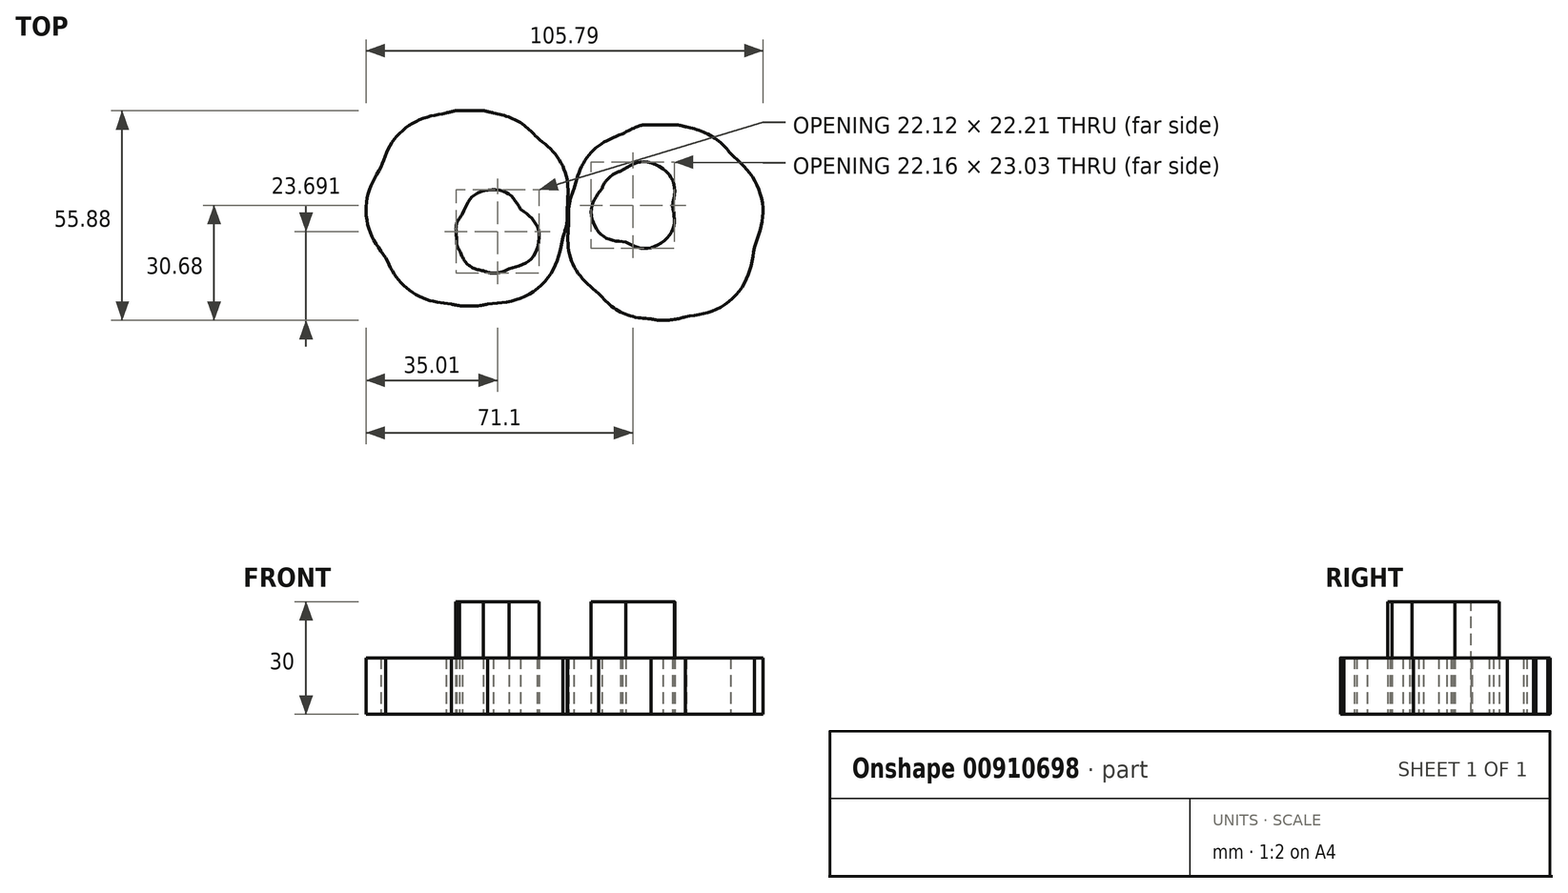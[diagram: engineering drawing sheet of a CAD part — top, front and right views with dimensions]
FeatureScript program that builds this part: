
annotation { "Feature Type Name" : "Feature", "Feature Type Description" : "" }
export const myFeature = defineFeature(function(context is Context, id is Id, definition is map)
    precondition{}
    {
        {
            var Q0;
            Q0=qCreatedBy(makeId("Top.planeOp"),FACE);
            var sketch = newSketch(context, id + "F0", { "sketchPlane" : qUnion([Q0])});
            skLineSegment(sketch, "E0", {"start": v(-95.48, 27.03) * mm, "end": v(-93.03, 29.79) * mm});
            skLineSegment(sketch, "E1", {"start": v(-93.03, 29.79) * mm, "end": v(-93.83, 30.39) * mm});
            skLineSegment(sketch, "E2", {"start": v(56.23, 54.56) * mm, "end": v(55.74, 53.41) * mm});
            skLineSegment(sketch, "E3", {"start": v(55.74, 53.41) * mm, "end": v(57.24, 52.44) * mm});
            skLineSegment(sketch, "E4", {"start": v(80.84, 41.38) * mm, "end": v(80.41, 40.74) * mm});
            skLineSegment(sketch, "E5", {"start": v(80.41, 40.74) * mm, "end": v(81.45, 40.47) * mm});
            skLineSegment(sketch, "E6", {"start": v(91.54, 26.28) * mm, "end": v(91, 26.08) * mm});
            skLineSegment(sketch, "E7", {"start": v(91, 26.08) * mm, "end": v(91.57, 24.93) * mm});
            skLineSegment(sketch, "E8", {"start": v(47.32, -84.2) * mm, "end": v(46.66, -83.57) * mm});
            skLineSegment(sketch, "E9", {"start": v(46.66, -83.57) * mm, "end": v(45.4, -85.45) * mm});
            skLineSegment(sketch, "E10", {"start": v(30.38, -92.46) * mm, "end": v(26.04, -92.61) * mm});
            skLineSegment(sketch, "E11", {"start": v(26.04, -92.61) * mm, "end": v(24.45, -94.1) * mm});
            skLineSegment(sketch, "E12", {"start": v(93.42, 9.92) * mm, "end": v(92.25, 12.13) * mm});
            skLineSegment(sketch, "E13", {"start": v(92.25, 12.13) * mm, "end": v(94.47, 11.99) * mm});
            skLineSegment(sketch, "E14", {"start": v(79.1, 38.53) * mm, "end": v(75.94, 39.15) * mm});
            skLineSegment(sketch, "E15", {"start": v(75.94, 39.15) * mm, "end": v(77.48, 40.95) * mm});
            skLineSegment(sketch, "E16", {"start": v(-43.97, 54.22) * mm, "end": v(-45.63, 56.72) * mm});
            skLineSegment(sketch, "E17", {"start": v(-45.63, 56.72) * mm, "end": v(-47.69, 56.87) * mm});
            skLineSegment(sketch, "E18", {"start": v(-94.6, 38.67) * mm, "end": v(-95.54, 38.86) * mm});
            skLineSegment(sketch, "E19", {"start": v(-95.54, 38.86) * mm, "end": v(-95.41, 37.43) * mm});
            skLineSegment(sketch, "E20", {"start": v(-81.53, -51.42) * mm, "end": v(-80.93, -50.2) * mm});
            skLineSegment(sketch, "E21", {"start": v(-80.93, -50.2) * mm, "end": v(-79.65, -54.72) * mm});
            skLineSegment(sketch, "E22", {"start": v(-52.24, -80.03) * mm, "end": v(-51.67, -79.57) * mm});
            skLineSegment(sketch, "E23", {"start": v(-51.67, -79.57) * mm, "end": v(-52.32, -78.88) * mm});
            skLineSegment(sketch, "E24", {"start": v(-83.46, 17.28) * mm, "end": v(-84.76, 19.09) * mm});
            skLineSegment(sketch, "E25", {"start": v(-84.76, 19.09) * mm, "end": v(-85.17, 18.4) * mm});
            skLineSegment(sketch, "E26", {"start": v(-83.81, 23.75) * mm, "end": v(-82.2, 23.79) * mm});
            skLineSegment(sketch, "E27", {"start": v(-82.2, 23.79) * mm, "end": v(-82.25, 21.9) * mm});
            skLineSegment(sketch, "E28", {"start": v(-34.26, 8.25) * mm, "end": v(-34.27, 7.59) * mm});
            skLineSegment(sketch, "E29", {"start": v(-34.27, 7.59) * mm, "end": v(-30.97, 7.59) * mm});
            skLineSegment(sketch, "E30", {"start": v(84.23, 4.65) * mm, "end": v(83.07, 5.79) * mm});
            skLineSegment(sketch, "E31", {"start": v(83.07, 5.79) * mm, "end": v(82.44, 4.95) * mm});
            skLineSegment(sketch, "E32", {"start": v(70.9, -1.37) * mm, "end": v(68.33, -1.9) * mm});
            skLineSegment(sketch, "E33", {"start": v(68.33, -1.9) * mm, "end": v(66.96, -4.53) * mm});
            skLineSegment(sketch, "E34", {"start": v(-1.99, -65.46) * mm, "end": v(-1.99, -65.46) * mm});
            skFitSpline(sketch, "E35", {"points": [v(6.05, -97.79) * mm, v(4.14, -97.5) * mm, v(2.63, -97.06) * mm, v(2.15, -96.63) * mm]});
            skFitSpline(sketch, "E36", {"points": [v(2.15, -96.63) * mm, v(1.78, -96.3) * mm, v(1.5, -96.31) * mm, v(-0.79, -96.78) * mm]});
            skFitSpline(sketch, "E37", {"points": [v(-0.79, -96.78) * mm, v(-5.54, -97.75) * mm, v(-11.38, -97.34) * mm, v(-19.87, -95.46) * mm]});
            skFitSpline(sketch, "E38", {"points": [v(-19.87, -95.46) * mm, v(-24.4, -94.46) * mm, v(-26.88, -93.53) * mm, v(-29.89, -91.7) * mm]});
            skFitSpline(sketch, "E39", {"points": [v(-29.89, -91.7) * mm, v(-31.74, -90.58) * mm, v(-32.75, -90.1) * mm, v(-33.02, -90.22) * mm]});
            skFitSpline(sketch, "E40", {"points": [v(-33.02, -90.22) * mm, v(-34.1, -90.66) * mm, v(-35.18, -90.77) * mm, v(-36.19, -90.53) * mm]});
            skFitSpline(sketch, "E41", {"points": [v(-36.19, -90.53) * mm, v(-38.87, -89.9) * mm, v(-43.88, -86.85) * mm, v(-47.32, -83.78) * mm]});
            skFitSpline(sketch, "E42", {"points": [v(-47.32, -83.78) * mm, v(-50.23, -81.18) * mm, v(-49.98, -81.3) * mm, v(-50.83, -82.01) * mm]});
            skFitSpline(sketch, "E43", {"points": [v(-50.83, -82.01) * mm, v(-51.67, -82.72) * mm, v(-53.21, -83.02) * mm, v(-54.97, -82.8) * mm]});
            skFitSpline(sketch, "E44", {"points": [v(-54.97, -82.8) * mm, v(-57.33, -82.53) * mm, v(-60.2, -80.23) * mm, v(-65.02, -74.79) * mm]});
            skFitSpline(sketch, "E45", {"points": [v(-65.02, -74.79) * mm, v(-66.5, -73.1) * mm, v(-67.85, -71.58) * mm, v(-68.02, -71.39) * mm]});
            skFitSpline(sketch, "E46", {"points": [v(-68.02, -71.39) * mm, v(-68.28, -71.1) * mm, v(-68.36, -71.14) * mm, v(-68.55, -71.63) * mm]});
            skFitSpline(sketch, "E47", {"points": [v(-68.55, -71.63) * mm, v(-69.1, -73.05) * mm, v(-70.94, -73.6) * mm, v(-72.26, -72.75) * mm]});
            skFitSpline(sketch, "E48", {"points": [v(-72.26, -72.75) * mm, v(-73.16, -72.16) * mm, v(-76.32, -68.49) * mm, v(-77.69, -66.44) * mm]});
            skFitSpline(sketch, "E49", {"points": [v(-77.69, -66.44) * mm, v(-78.97, -64.52) * mm, v(-79.65, -62.88) * mm, v(-81.02, -58.41) * mm]});
            skFitSpline(sketch, "E50", {"points": [v(-81.02, -58.41) * mm, v(-81.9, -55.54) * mm, v(-81.96, -55.4) * mm, v(-82.71, -55.16) * mm]});
            skFitSpline(sketch, "E51", {"points": [v(-82.71, -55.16) * mm, v(-83.82, -54.8) * mm, v(-84.43, -54.07) * mm, v(-86.12, -51.11) * mm]});
            skFitSpline(sketch, "E52", {"points": [v(-86.12, -51.11) * mm, v(-89.94, -44.44) * mm, v(-90.7, -41.83) * mm, v(-91.66, -32.31) * mm]});
            skFitSpline(sketch, "E53", {"points": [v(-91.66, -32.31) * mm, v(-91.82, -30.7) * mm, v(-92.03, -29.37) * mm, v(-92.12, -29.37) * mm]});
            skFitSpline(sketch, "E54", {"points": [v(-92.12, -29.37) * mm, v(-92.21, -29.37) * mm, v(-93.03, -29.8) * mm, v(-93.94, -30.32) * mm]});
            skFitSpline(sketch, "E55", {"points": [v(-93.94, -30.32) * mm, v(-95.84, -31.41) * mm, v(-99.04, -32.54) * mm, v(-100.23, -32.54) * mm]});
            skFitSpline(sketch, "E56", {"points": [v(-100.23, -32.54) * mm, v(-101.33, -32.54) * mm, v(-102.26, -31.8) * mm, v(-102.53, -30.72) * mm]});
            skFitSpline(sketch, "E57", {"points": [v(-102.53, -30.72) * mm, v(-102.74, -29.9) * mm, v(-102.63, -29.57) * mm, v(-101.04, -26.3) * mm]});
            skFitSpline(sketch, "E58", {"points": [v(-101.04, -26.3) * mm, v(-100.1, -24.36) * mm, v(-99.15, -22.23) * mm, v(-98.92, -21.57) * mm]});
            skFitSpline(sketch, "E59", {"points": [v(-98.92, -21.57) * mm, v(-98.32, -19.8) * mm, v(-98.43, -16.76) * mm, v(-99.29, -11.54) * mm]});
            skFitSpline(sketch, "E60", {"points": [v(-99.29, -11.54) * mm, v(-100.31, -5.31) * mm, v(-100.38, -4.25) * mm, v(-99.94, -1.18) * mm]});
            skFitSpline(sketch, "E61", {"points": [v(-99.94, -1.18) * mm, v(-99.74, 0.27) * mm, v(-99.6, 1.48) * mm, v(-99.65, 1.53) * mm]});
            skFitSpline(sketch, "E62", {"points": [v(-99.65, 1.53) * mm, v(-99.69, 1.57) * mm, v(-100.03, 1.48) * mm, v(-100.41, 1.34) * mm]});
            skFitSpline(sketch, "E63", {"points": [v(-100.41, 1.34) * mm, v(-101.82, 0.8) * mm, v(-103.37, 1.61) * mm, v(-103.71, 3.05) * mm]});
            skFitSpline(sketch, "E64", {"points": [v(-103.71, 3.05) * mm, v(-103.97, 4.14) * mm, v(-100.97, 17.98) * mm, v(-99.82, 21) * mm]});
            skFitSpline(sketch, "E65", {"points": [v(-99.82, 21) * mm, v(-99.22, 22.58) * mm, v(-98.33, 23.82) * mm, v(-95.48, 27.03) * mm]});
            skFitSpline(sketch, "E66", {"points": [v(-93.83, 30.39) * mm, v(-95.91, 31.94) * mm, v(-96.84, 33.33) * mm, v(-97.51, 35.92) * mm]});
            skFitSpline(sketch, "E67", {"points": [v(-97.51, 35.92) * mm, v(-98.3, 38.9) * mm, v(-97.56, 40.94) * mm, v(-95.7, 41) * mm]});
            skFitSpline(sketch, "E68", {"points": [v(-95.7, 41) * mm, v(-95.24, 41.03) * mm, v(-93.74, 40.9) * mm, v(-92.36, 40.72) * mm]});
            skFitSpline(sketch, "E69", {"points": [v(-92.36, 40.72) * mm, v(-87.83, 40.15) * mm, v(-83.3, 40.79) * mm, v(-79.67, 42.5) * mm]});
            skFitSpline(sketch, "E70", {"points": [v(-79.67, 42.5) * mm, v(-77.94, 43.33) * mm, v(-77.62, 43.83) * mm, v(-78.84, 43.83) * mm]});
            skFitSpline(sketch, "E71", {"points": [v(-78.84, 43.83) * mm, v(-79.85, 43.83) * mm, v(-81.26, 44.34) * mm, v(-81.8, 44.9) * mm]});
            skFitSpline(sketch, "E72", {"points": [v(-81.8, 44.9) * mm, v(-83.07, 46.27) * mm, v(-82.51, 48.3) * mm, v(-80.42, 49.94) * mm]});
            skFitSpline(sketch, "E73", {"points": [v(-80.42, 49.94) * mm, v(-76.42, 53.08) * mm, v(-71.34, 55.19) * mm, v(-66.49, 55.72) * mm]});
            skFitSpline(sketch, "E74", {"points": [v(-66.49, 55.72) * mm, v(-64.9, 55.9) * mm, v(-64.88, 55.92) * mm, v(-65.21, 57.34) * mm]});
            skFitSpline(sketch, "E75", {"points": [v(-65.21, 57.34) * mm, v(-65.65, 59.22) * mm, v(-63.92, 62.87) * mm, v(-62.2, 63.69) * mm]});
            skFitSpline(sketch, "E76", {"points": [v(-62.2, 63.69) * mm, v(-61.14, 64.2) * mm, v(-59.85, 63.92) * mm, v(-59.2, 63.04) * mm]});
            skFitSpline(sketch, "E77", {"points": [v(-59.2, 63.04) * mm, v(-58.54, 62.14) * mm, v(-55.62, 60.81) * mm, v(-52.6, 60.02) * mm]});
            skFitSpline(sketch, "E78", {"points": [v(-52.6, 60.02) * mm, v(-49.95, 59.34) * mm, v(-46.75, 58.98) * mm, v(-46.75, 59.36) * mm]});
            skFitSpline(sketch, "E79", {"points": [v(-46.75, 59.36) * mm, v(-46.75, 59.5) * mm, v(-46.92, 60.08) * mm, v(-47.12, 60.66) * mm]});
            skFitSpline(sketch, "E80", {"points": [v(-47.12, 60.66) * mm, v(-48.58, 64.8) * mm, v(-49, 71.08) * mm, v(-48.1, 75.27) * mm]});
            skFitSpline(sketch, "E81", {"points": [v(-48.1, 75.27) * mm, v(-47.2, 79.44) * mm, v(-45.9, 82.5) * mm, v(-43.58, 85.88) * mm]});
            skFitSpline(sketch, "E82", {"points": [v(-43.58, 85.88) * mm, v(-39.81, 91.4) * mm, v(-34.08, 95.4) * mm, v(-27.41, 97.16) * mm]});
            skFitSpline(sketch, "E83", {"points": [v(-27.41, 97.16) * mm, v(-24.72, 97.87) * mm, v(-24.3, 97.92) * mm, v(-20.35, 97.92) * mm]});
            skFitSpline(sketch, "E84", {"points": [v(-20.35, 97.92) * mm, v(-16.41, 97.92) * mm, v(-15.97, 97.87) * mm, v(-13.34, 97.17) * mm]});
            skFitSpline(sketch, "E85", {"points": [v(-13.34, 97.17) * mm, v(-6.67, 95.4) * mm, v(-0.85, 91.33) * mm, v(2.97, 85.76) * mm]});
            skFitSpline(sketch, "E86", {"points": [v(2.97, 85.76) * mm, v(4.3, 83.8) * mm, v(6.3, 79.99) * mm, v(6.3, 79.37) * mm]});
            skFitSpline(sketch, "E87", {"points": [v(6.3, 79.37) * mm, v(6.3, 78.77) * mm, v(6.77, 79.19) * mm, v(7.44, 80.38) * mm]});
            skFitSpline(sketch, "E88", {"points": [v(7.44, 80.38) * mm, v(14.63, 93.12) * mm, v(30.6, 97.96) * mm, v(43.5, 91.32) * mm]});
            skFitSpline(sketch, "E89", {"points": [v(43.5, 91.32) * mm, v(48.62, 88.68) * mm, v(53.1, 84.04) * mm, v(55.63, 78.75) * mm]});
            skFitSpline(sketch, "E90", {"points": [v(55.63, 78.75) * mm, v(57.4, 75.03) * mm, v(58.6, 69.9) * mm, v(58.6, 66.03) * mm]});
            skFitSpline(sketch, "E91", {"points": [v(58.6, 66.03) * mm, v(58.6, 62.77) * mm, v(57.54, 57.6) * mm, v(56.23, 54.56) * mm]});
            skFitSpline(sketch, "E92", {"points": [v(57.24, 52.44) * mm, v(58.94, 51.34) * mm, v(61.12, 50.26) * mm, v(63.12, 49.54) * mm]});
            skFitSpline(sketch, "E93", {"points": [v(63.12, 49.54) * mm, v(65.07, 48.83) * mm, v(71.4, 48.66) * mm, v(75.82, 49.2) * mm]});
            skFitSpline(sketch, "E94", {"points": [v(75.82, 49.2) * mm, v(77.57, 49.42) * mm, v(79.36, 49.59) * mm, v(79.8, 49.59) * mm]});
            skFitSpline(sketch, "E95", {"points": [v(79.8, 49.59) * mm, v(80.97, 49.59) * mm, v(81.76, 48.72) * mm, v(82.09, 47.06) * mm]});
            skFitSpline(sketch, "E96", {"points": [v(82.09, 47.06) * mm, v(82.48, 45.1) * mm, v(82.08, 43.26) * mm, v(80.84, 41.38) * mm]});
            skFitSpline(sketch, "E97", {"points": [v(81.45, 40.47) * mm, v(84.65, 39.64) * mm, v(86.46, 38.97) * mm, v(87.31, 38.3) * mm]});
            skFitSpline(sketch, "E98", {"points": [v(87.31, 38.3) * mm, v(89.54, 36.53) * mm, v(92.98, 30.66) * mm, v(93.03, 28.57) * mm]});
            skFitSpline(sketch, "E99", {"points": [v(93.03, 28.57) * mm, v(93.05, 27.47) * mm, v(92.52, 26.66) * mm, v(91.54, 26.28) * mm]});
            skFitSpline(sketch, "E100", {"points": [v(91.57, 24.93) * mm, v(91.88, 24.3) * mm, v(92.43, 23) * mm, v(92.8, 22.05) * mm]});
            skFitSpline(sketch, "E101", {"points": [v(92.8, 22.05) * mm, v(93.65, 19.78) * mm, v(94.74, 18.82) * mm, v(98.58, 16.95) * mm]});
            skFitSpline(sketch, "E102", {"points": [v(98.58, 16.95) * mm, v(101.15, 15.7) * mm, v(101.55, 15.42) * mm, v(101.79, 14.75) * mm]});
            skFitSpline(sketch, "E103", {"points": [v(101.79, 14.75) * mm, v(102.2, 13.59) * mm, v(101.88, 12.51) * mm, v(100.83, 11.46) * mm]});
            skFitSpline(sketch, "E104", {"points": [v(100.83, 11.46) * mm, v(99.86, 10.5) * mm, v(99.28, 10.2) * mm, v(97.55, 9.75) * mm]});
            skFitSpline(sketch, "E105", {"points": [v(97.55, 9.75) * mm, v(96.99, 9.6) * mm, v(96.53, 9.41) * mm, v(96.53, 9.32) * mm]});
            skFitSpline(sketch, "E106", {"points": [v(96.53, 9.32) * mm, v(96.53, 9.22) * mm, v(96.9, 8.2) * mm, v(97.35, 7.06) * mm]});
            skFitSpline(sketch, "E107", {"points": [v(97.35, 7.06) * mm, v(97.8, 5.91) * mm, v(98.39, 4.08) * mm, v(98.66, 2.98) * mm]});
            skFitSpline(sketch, "E108", {"points": [v(98.66, 2.98) * mm, v(99.43, -0.2) * mm, v(100.66, -8.05) * mm, v(100.5, -8.87) * mm]});
            skFitSpline(sketch, "E109", {"points": [v(100.5, -8.87) * mm, v(100.24, -10.27) * mm, v(98.77, -11.09) * mm, v(97.27, -10.66) * mm]});
            skFitSpline(sketch, "E110", {"points": [v(97.27, -10.66) * mm, v(96.5, -10.44) * mm, v(96.49, -10.44) * mm, v(96.64, -11.08) * mm]});
            skFitSpline(sketch, "E111", {"points": [v(96.64, -11.08) * mm, v(96.73, -11.44) * mm, v(97.15, -12.43) * mm, v(97.57, -13.28) * mm]});
            skFitSpline(sketch, "E112", {"points": [v(97.57, -13.28) * mm, v(98.27, -14.72) * mm, v(98.48, -14.93) * mm, v(100.37, -16.1) * mm]});
            skFitSpline(sketch, "E113", {"points": [v(100.37, -16.1) * mm, v(103.64, -18.1) * mm, v(104.23, -19.08) * mm, v(103.38, -21.1) * mm]});
            skFitSpline(sketch, "E114", {"points": [v(103.38, -21.1) * mm, v(102.01, -24.38) * mm, v(99, -25.51) * mm, v(94.66, -24.39) * mm]});
            skFitSpline(sketch, "E115", {"points": [v(94.66, -24.39) * mm, v(93.7, -24.14) * mm, v(92.87, -24) * mm, v(92.82, -24.07) * mm]});
            skFitSpline(sketch, "E116", {"points": [v(92.82, -24.07) * mm, v(92.77, -24.15) * mm, v(92.61, -25.9) * mm, v(92.46, -27.93) * mm]});
            skFitSpline(sketch, "E117", {"points": [v(92.46, -27.93) * mm, v(92.03, -33.93) * mm, v(91.32, -37.41) * mm, v(90.03, -39.97) * mm]});
            skFitSpline(sketch, "E118", {"points": [v(90.03, -39.97) * mm, v(89.16, -41.69) * mm, v(88.07, -42.82) * mm, v(85.85, -44.28) * mm]});
            skFitSpline(sketch, "E119", {"points": [v(85.85, -44.28) * mm, v(83.52, -45.8) * mm, v(82.66, -46.22) * mm, v(81.74, -46.24) * mm]});
            skFitSpline(sketch, "E120", {"points": [v(81.74, -46.24) * mm, v(80.97, -46.27) * mm, v(80.92, -46.33) * mm, v(80.42, -47.84) * mm]});
            skFitSpline(sketch, "E121", {"points": [v(80.42, -47.84) * mm, v(79.78, -49.8) * mm, v(78.94, -51.5) * mm, v(77.93, -52.9) * mm]});
            skFitSpline(sketch, "E122", {"points": [v(77.93, -52.9) * mm, v(75.96, -55.62) * mm, v(75.45, -57.28) * mm, v(74, -65.78) * mm]});
            skFitSpline(sketch, "E123", {"points": [v(74, -65.78) * mm, v(73.46, -68.85) * mm, v(72.91, -71.59) * mm, v(72.76, -71.87) * mm]});
            skFitSpline(sketch, "E124", {"points": [v(72.76, -71.87) * mm, v(72.61, -72.14) * mm, v(72.13, -72.52) * mm, v(71.68, -72.71) * mm]});
            skFitSpline(sketch, "E125", {"points": [v(71.68, -72.71) * mm, v(70.36, -73.26) * mm, v(69.1, -73.14) * mm, v(66.97, -72.23) * mm]});
            skFitSpline(sketch, "E126", {"points": [v(66.97, -72.23) * mm, v(66.66, -72.1) * mm, v(66.4, -72.39) * mm, v(65.77, -73.57) * mm]});
            skFitSpline(sketch, "E127", {"points": [v(65.77, -73.57) * mm, v(64.13, -76.66) * mm, v(60.82, -79.23) * mm, v(53.73, -82.9) * mm]});
            skFitSpline(sketch, "E128", {"points": [v(53.73, -82.9) * mm, v(49.4, -85.15) * mm, v(48.5, -85.33) * mm, v(47.32, -84.2) * mm]});
            skFitSpline(sketch, "E129", {"points": [v(45.4, -85.45) * mm, v(42.86, -89.22) * mm, v(40.28, -91.1) * mm, v(36.53, -91.92) * mm]});
            skFitSpline(sketch, "E130", {"points": [v(36.53, -91.92) * mm, v(35.46, -92.15) * mm, v(32.96, -92.37) * mm, v(30.38, -92.46) * mm]});
            skFitSpline(sketch, "E131", {"points": [v(24.45, -94.1) * mm, v(21.43, -96.92) * mm, v(18.58, -97.77) * mm, v(11.7, -97.9) * mm]});
            skFitSpline(sketch, "E132", {"points": [v(11.7, -97.9) * mm, v(9.31, -97.94) * mm, v(6.78, -97.9) * mm, v(6.05, -97.79) * mm]});
            skFitSpline(sketch, "E133", {"points": [v(17.45, -95.13) * mm, v(19.61, -94.7) * mm, v(21.29, -93.8) * mm, v(23.11, -92.08) * mm]});
            skFitSpline(sketch, "E134", {"points": [v(23.11, -92.08) * mm, v(24.24, -91.02) * mm, v(25.05, -90.46) * mm, v(25.66, -90.31) * mm]});
            skFitSpline(sketch, "E135", {"points": [v(25.66, -90.31) * mm, v(26.16, -90.2) * mm, v(28.14, -90.1) * mm, v(30.05, -90.09) * mm]});
            skFitSpline(sketch, "E136", {"points": [v(30.05, -90.09) * mm, v(35.63, -90.07) * mm, v(38.51, -89.33) * mm, v(40.8, -87.34) * mm]});
            skFitSpline(sketch, "E137", {"points": [v(40.8, -87.34) * mm, v(41.36, -86.84) * mm, v(42.65, -85.18) * mm, v(43.66, -83.65) * mm]});
            skFitSpline(sketch, "E138", {"points": [v(43.66, -83.65) * mm, v(44.67, -82.1) * mm, v(45.87, -80.4) * mm, v(46.31, -79.84) * mm]});
            skFitSpline(sketch, "E139", {"points": [v(46.31, -79.84) * mm, v(47.24, -78.7) * mm, v(50.4, -76.04) * mm, v(50.6, -76.24) * mm]});
            skFitSpline(sketch, "E140", {"points": [v(50.6, -76.24) * mm, v(50.67, -76.3) * mm, v(50.34, -77.69) * mm, v(49.86, -79.3) * mm]});
            skFitSpline(sketch, "E141", {"points": [v(49.86, -79.3) * mm, v(49.38, -80.91) * mm, v(49.05, -82.3) * mm, v(49.14, -82.38) * mm]});
            skFitSpline(sketch, "E142", {"points": [v(49.14, -82.38) * mm, v(49.48, -82.72) * mm, v(57.35, -78.35) * mm, v(60.4, -76.13) * mm]});
            skFitSpline(sketch, "E143", {"points": [v(60.4, -76.13) * mm, v(62.95, -74.27) * mm, v(64.48, -71.65) * mm, v(65.64, -67.15) * mm]});
            skFitSpline(sketch, "E144", {"points": [v(65.64, -67.15) * mm, v(65.93, -66.04) * mm, v(66.24, -65.13) * mm, v(66.32, -65.13) * mm]});
            skFitSpline(sketch, "E145", {"points": [v(66.32, -65.13) * mm, v(66.53, -65.13) * mm, v(67.4, -67.39) * mm, v(67.75, -68.8) * mm]});
            skFitSpline(sketch, "E146", {"points": [v(67.75, -68.8) * mm, v(67.91, -69.45) * mm, v(68.25, -70.1) * mm, v(68.53, -70.3) * mm]});
            skFitSpline(sketch, "E147", {"points": [v(68.53, -70.3) * mm, v(69.05, -70.66) * mm, v(70.85, -70.8) * mm, v(70.85, -70.47) * mm]});
            skFitSpline(sketch, "E148", {"points": [v(70.85, -70.47) * mm, v(70.85, -70.05) * mm, v(72.1, -62.85) * mm, v(72.67, -60.02) * mm]});
            skFitSpline(sketch, "E149", {"points": [v(72.67, -60.02) * mm, v(73.49, -55.94) * mm, v(73.94, -54.7) * mm, v(75.52, -52.28) * mm]});
            skFitSpline(sketch, "E150", {"points": [v(75.52, -52.28) * mm, v(77.22, -49.66) * mm, v(77.6, -48.89) * mm, v(78.4, -46.41) * mm]});
            skFitSpline(sketch, "E151", {"points": [v(78.4, -46.41) * mm, v(79.14, -44.1) * mm, v(80.9, -40.17) * mm, v(81.2, -40.17) * mm]});
            skFitSpline(sketch, "E152", {"points": [v(81.2, -40.17) * mm, v(81.32, -40.17) * mm, v(81.41, -40.96) * mm, v(81.41, -41.93) * mm]});
            skFitSpline(sketch, "E153", {"points": [v(81.41, -41.93) * mm, v(81.41, -42.9) * mm, v(81.48, -43.76) * mm, v(81.57, -43.85) * mm]});
            skFitSpline(sketch, "E154", {"points": [v(81.57, -43.85) * mm, v(81.76, -44.04) * mm, v(83.36, -43.14) * mm, v(85.4, -41.7) * mm]});
            skFitSpline(sketch, "E155", {"points": [v(85.4, -41.7) * mm, v(88.64, -39.42) * mm, v(89.56, -36.52) * mm, v(90.2, -26.56) * mm]});
            skFitSpline(sketch, "E156", {"points": [v(90.2, -26.56) * mm, v(90.4, -23.29) * mm, v(90.6, -20.57) * mm, v(90.65, -20.53) * mm]});
            skFitSpline(sketch, "E157", {"points": [v(90.65, -20.53) * mm, v(90.7, -20.48) * mm, v(91.53, -20.76) * mm, v(92.5, -21.15) * mm]});
            skFitSpline(sketch, "E158", {"points": [v(92.5, -21.15) * mm, v(96.2, -22.65) * mm, v(98.05, -22.87) * mm, v(99.72, -22.01) * mm]});
            skFitSpline(sketch, "E159", {"points": [v(99.72, -22.01) * mm, v(100.42, -21.65) * mm, v(101.33, -20.39) * mm, v(101.33, -19.77) * mm]});
            skFitSpline(sketch, "E160", {"points": [v(101.33, -19.77) * mm, v(101.33, -19.43) * mm, v(99.46, -18.1) * mm, v(97.79, -17.27) * mm]});
            skFitSpline(sketch, "E161", {"points": [v(97.79, -17.27) * mm, v(96.19, -16.47) * mm, v(94.9, -13.88) * mm, v(93.32, -8.3) * mm]});
            skFitSpline(sketch, "E162", {"points": [v(93.32, -8.3) * mm, v(92.01, -3.69) * mm, v(92.01, -3.93) * mm, v(93.34, -5.33) * mm]});
            skFitSpline(sketch, "E163", {"points": [v(93.34, -5.33) * mm, v(94, -6.03) * mm, v(95.27, -6.96) * mm, v(96.35, -7.54) * mm]});
            skFitSpline(sketch, "E164", {"points": [v(96.35, -7.54) * mm, v(98.18, -8.52) * mm, v(98.21, -8.52) * mm, v(98.2, -7.97) * mm]});
            skFitSpline(sketch, "E165", {"points": [v(98.2, -7.97) * mm, v(98.2, -7.35) * mm, v(96.9, 0.5) * mm, v(96.52, 2.22) * mm]});
            skFitSpline(sketch, "E166", {"points": [v(96.52, 2.22) * mm, v(96.14, 3.91) * mm, v(94.71, 7.46) * mm, v(93.42, 9.92) * mm]});
            skFitSpline(sketch, "E167", {"points": [v(94.47, 11.99) * mm, v(96.85, 11.83) * mm, v(97.96, 12.05) * mm, v(99.04, 12.9) * mm]});
            skFitSpline(sketch, "E168", {"points": [v(99.04, 12.9) * mm, v(99.37, 13.17) * mm, v(99.65, 13.51) * mm, v(99.64, 13.67) * mm]});
            skFitSpline(sketch, "E169", {"points": [v(99.64, 13.67) * mm, v(99.64, 13.82) * mm, v(98.34, 14.58) * mm, v(96.76, 15.35) * mm]});
            skFitSpline(sketch, "E170", {"points": [v(96.76, 15.35) * mm, v(92.93, 17.2) * mm, v(91.67, 18.41) * mm, v(90.59, 21.27) * mm]});
            skFitSpline(sketch, "E171", {"points": [v(90.59, 21.27) * mm, v(90.16, 22.4) * mm, v(89.12, 24.55) * mm, v(88.28, 26.07) * mm]});
            skFitSpline(sketch, "E172", {"points": [v(88.28, 26.07) * mm, v(87.43, 27.59) * mm, v(86.75, 28.85) * mm, v(86.78, 28.87) * mm]});
            skFitSpline(sketch, "E173", {"points": [v(86.78, 28.87) * mm, v(86.8, 28.9) * mm, v(87.65, 28.8) * mm, v(88.68, 28.66) * mm]});
            skFitSpline(sketch, "E174", {"points": [v(88.68, 28.66) * mm, v(89.7, 28.51) * mm, v(90.6, 28.47) * mm, v(90.7, 28.56) * mm]});
            skFitSpline(sketch, "E175", {"points": [v(90.7, 28.56) * mm, v(90.92, 28.78) * mm, v(89.44, 31.8) * mm, v(88.1, 33.87) * mm]});
            skFitSpline(sketch, "E176", {"points": [v(88.1, 33.87) * mm, v(86.16, 36.87) * mm, v(85.37, 37.28) * mm, v(79.1, 38.53) * mm]});
            skFitSpline(sketch, "E177", {"points": [v(77.48, 40.95) * mm, v(79.33, 43.12) * mm, v(79.97, 44.35) * mm, v(79.97, 45.76) * mm]});
            skFitSpline(sketch, "E178", {"points": [v(79.97, 45.76) * mm, v(79.96, 47.47) * mm, v(79.94, 47.48) * mm, v(76.96, 47.04) * mm]});
            skFitSpline(sketch, "E179", {"points": [v(76.96, 47.04) * mm, v(75.28, 46.79) * mm, v(72.68, 46.64) * mm, v(69.77, 46.63) * mm]});
            skFitSpline(sketch, "E180", {"points": [v(69.77, 46.63) * mm, v(65.86, 46.62) * mm, v(64.95, 46.7) * mm, v(63.4, 47.12) * mm]});
            skFitSpline(sketch, "E181", {"points": [v(63.4, 47.12) * mm, v(61.28, 47.71) * mm, v(58.06, 49.16) * mm, v(56.1, 50.4) * mm]});
            skFitSpline(sketch, "E182", {"points": [v(56.1, 50.4) * mm, v(55.34, 50.9) * mm, v(54.63, 51.21) * mm, v(54.54, 51.1) * mm]});
            skFitSpline(sketch, "E183", {"points": [v(54.54, 51.1) * mm, v(54.45, 51) * mm, v(53.85, 50.15) * mm, v(53.2, 49.23) * mm]});
            skFitSpline(sketch, "E184", {"points": [v(53.2, 49.23) * mm, v(50.66, 45.58) * mm, v(46.06, 41.8) * mm, v(42.05, 40.06) * mm]});
            skFitSpline(sketch, "E185", {"points": [v(42.05, 40.06) * mm, v(41, 39.62) * mm, v(39.1, 38.96) * mm, v(37.8, 38.61) * mm]});
            skFitSpline(sketch, "E186", {"points": [v(37.8, 38.61) * mm, v(35.7, 38.05) * mm, v(35.01, 37.98) * mm, v(31.25, 37.97) * mm]});
            skFitSpline(sketch, "E187", {"points": [v(31.25, 37.97) * mm, v(27.66, 37.95) * mm, v(26.74, 38.03) * mm, v(24.93, 38.5) * mm]});
            skFitSpline(sketch, "E188", {"points": [v(24.93, 38.5) * mm, v(18.06, 40.24) * mm, v(12.56, 44.1) * mm, v(8.58, 49.93) * mm]});
            skFitSpline(sketch, "E189", {"points": [v(8.58, 49.93) * mm, v(7.26, 51.88) * mm, v(6, 54.33) * mm, v(5.56, 55.78) * mm]});
            skFitSpline(sketch, "E190", {"points": [v(5.56, 55.78) * mm, v(5.39, 56.34) * mm, v(5.17, 56.77) * mm, v(5.07, 56.74) * mm]});
            skFitSpline(sketch, "E191", {"points": [v(5.07, 56.74) * mm, v(4.97, 56.7) * mm, v(4.23, 55.67) * mm, v(3.43, 54.45) * mm]});
            skFitSpline(sketch, "E192", {"points": [v(3.43, 54.45) * mm, v(-0.23, 48.86) * mm, v(-6, 44.5) * mm, v(-12.06, 42.75) * mm]});
            skFitSpline(sketch, "E193", {"points": [v(-12.06, 42.75) * mm, v(-17.97, 41.05) * mm, v(-22.71, 41.04) * mm, v(-28.52, 42.72) * mm]});
            skFitSpline(sketch, "E194", {"points": [v(-28.52, 42.72) * mm, v(-34.7, 44.52) * mm, v(-40.33, 48.7) * mm, v(-43.97, 54.22) * mm]});
            skFitSpline(sketch, "E195", {"points": [v(-47.69, 56.87) * mm, v(-50.78, 57.1) * mm, v(-56.17, 58.5) * mm, v(-58.56, 59.7) * mm]});
            skFitSpline(sketch, "E196", {"points": [v(-58.56, 59.7) * mm, v(-59.05, 59.95) * mm, v(-59.84, 60.49) * mm, v(-60.3, 60.9) * mm]});
            skFitSpline(sketch, "E197", {"points": [v(-60.3, 60.9) * mm, v(-61.32, 61.78) * mm, v(-61.58, 61.66) * mm, v(-62.49, 59.87) * mm]});
            skFitSpline(sketch, "E198", {"points": [v(-62.49, 59.87) * mm, v(-63.55, 57.77) * mm, v(-63.37, 57.4) * mm, v(-60.2, 55.13) * mm]});
            skFitSpline(sketch, "E199", {"points": [v(-60.2, 55.13) * mm, v(-58.9, 54.2) * mm, v(-57.76, 53.34) * mm, v(-57.7, 53.23) * mm]});
            skFitSpline(sketch, "E200", {"points": [v(-57.7, 53.23) * mm, v(-57.63, 53.13) * mm, v(-58.35, 53.14) * mm, v(-59.3, 53.25) * mm]});
            skFitSpline(sketch, "E201", {"points": [v(-59.3, 53.25) * mm, v(-60.25, 53.37) * mm, v(-62.76, 53.42) * mm, v(-64.87, 53.37) * mm]});
            skFitSpline(sketch, "E202", {"points": [v(-64.87, 53.37) * mm, v(-68.25, 53.28) * mm, v(-68.93, 53.2) * mm, v(-70.58, 52.63) * mm]});
            skFitSpline(sketch, "E203", {"points": [v(-70.58, 52.63) * mm, v(-75.15, 51.06) * mm, v(-80.45, 47.7) * mm, v(-80.04, 46.62) * mm]});
            skFitSpline(sketch, "E204", {"points": [v(-80.04, 46.62) * mm, v(-79.94, 46.38) * mm, v(-79.34, 46.22) * mm, v(-78.03, 46.11) * mm]});
            skFitSpline(sketch, "E205", {"points": [v(-78.03, 46.11) * mm, v(-74.17, 45.79) * mm, v(-72.43, 45.34) * mm, v(-72.43, 44.68) * mm]});
            skFitSpline(sketch, "E206", {"points": [v(-72.43, 44.68) * mm, v(-72.43, 43.56) * mm, v(-78.87, 39.94) * mm, v(-82.5, 39.01) * mm]});
            skFitSpline(sketch, "E207", {"points": [v(-82.5, 39.01) * mm, v(-85.77, 38.2) * mm, v(-91.4, 38.03) * mm, v(-94.6, 38.67) * mm]});
            skFitSpline(sketch, "E208", {"points": [v(-95.41, 37.43) * mm, v(-95.26, 35.69) * mm, v(-94.33, 33.76) * mm, v(-93.25, 32.94) * mm]});
            skFitSpline(sketch, "E209", {"points": [v(-93.25, 32.94) * mm, v(-92.4, 32.3) * mm, v(-89.82, 30.7) * mm, v(-89.38, 30.56) * mm]});
            skFitSpline(sketch, "E210", {"points": [v(-89.38, 30.56) * mm, v(-89.23, 30.5) * mm, v(-90.36, 29.13) * mm, v(-91.88, 27.49) * mm]});
            skFitSpline(sketch, "E211", {"points": [v(-91.88, 27.49) * mm, v(-97.27, 21.7) * mm, v(-97.46, 21.4) * mm, v(-98.7, 16.67) * mm]});
            skFitSpline(sketch, "E212", {"points": [v(-98.7, 16.67) * mm, v(-99.54, 13.44) * mm, v(-101.22, 5.44) * mm, v(-101.23, 4.63) * mm]});
            skFitSpline(sketch, "E213", {"points": [v(-101.23, 4.63) * mm, v(-101.23, 4.28) * mm, v(-100.96, 4.41) * mm, v(-99.97, 5.24) * mm]});
            skFitSpline(sketch, "E214", {"points": [v(-99.97, 5.24) * mm, v(-97.91, 6.96) * mm, v(-96.65, 7.9) * mm, v(-96.54, 7.78) * mm]});
            skFitSpline(sketch, "E215", {"points": [v(-96.54, 7.78) * mm, v(-96.48, 7.72) * mm, v(-96.72, 5.52) * mm, v(-97.08, 2.9) * mm]});
            skFitSpline(sketch, "E216", {"points": [v(-97.08, 2.9) * mm, v(-97.95, -3.59) * mm, v(-97.92, -6) * mm, v(-96.93, -11.85) * mm]});
            skFitSpline(sketch, "E217", {"points": [v(-96.93, -11.85) * mm, v(-95.66, -19.34) * mm, v(-95.94, -21.51) * mm, v(-98.92, -27.33) * mm]});
            skFitSpline(sketch, "E218", {"points": [v(-98.92, -27.33) * mm, v(-99.6, -28.65) * mm, v(-100.19, -29.83) * mm, v(-100.24, -29.95) * mm]});
            skFitSpline(sketch, "E219", {"points": [v(-100.24, -29.95) * mm, v(-100.43, -30.4) * mm, v(-98.44, -29.84) * mm, v(-96.51, -28.91) * mm]});
            skFitSpline(sketch, "E220", {"points": [v(-96.51, -28.91) * mm, v(-94.17, -27.79) * mm, v(-92.07, -26.4) * mm, v(-90.92, -25.2) * mm]});
            skFitSpline(sketch, "E221", {"points": [v(-90.92, -25.2) * mm, v(-90.47, -24.72) * mm, v(-90.03, -24.33) * mm, v(-89.94, -24.33) * mm]});
            skFitSpline(sketch, "E222", {"points": [v(-89.94, -24.33) * mm, v(-89.85, -24.33) * mm, v(-89.7, -25.82) * mm, v(-89.62, -27.63) * mm]});
            skFitSpline(sketch, "E223", {"points": [v(-89.62, -27.63) * mm, v(-89.4, -32.18) * mm, v(-88.82, -37.43) * mm, v(-88.25, -40.3) * mm]});
            skFitSpline(sketch, "E224", {"points": [v(-88.25, -40.3) * mm, v(-87.9, -42.02) * mm, v(-87.4, -43.44) * mm, v(-86.47, -45.39) * mm]});
            skFitSpline(sketch, "E225", {"points": [v(-86.47, -45.39) * mm, v(-85.03, -48.4) * mm, v(-82.6, -52.65) * mm, v(-82.31, -52.65) * mm]});
            skFitSpline(sketch, "E226", {"points": [v(-82.31, -52.65) * mm, v(-82.21, -52.65) * mm, v(-81.86, -52.1) * mm, v(-81.53, -51.42) * mm]});
            skFitSpline(sketch, "E227", {"points": [v(-79.65, -54.72) * mm, v(-77.9, -60.9) * mm, v(-77.13, -62.93) * mm, v(-75.8, -64.96) * mm]});
            skFitSpline(sketch, "E228", {"points": [v(-75.8, -64.96) * mm, v(-74.6, -66.78) * mm, v(-71.34, -70.65) * mm, v(-71.01, -70.65) * mm]});
            skFitSpline(sketch, "E229", {"points": [v(-71.01, -70.65) * mm, v(-70.9, -70.65) * mm, v(-70.57, -69.76) * mm, v(-70.28, -68.67) * mm]});
            skFitSpline(sketch, "E230", {"points": [v(-70.28, -68.67) * mm, v(-69.98, -67.58) * mm, v(-69.7, -66.54) * mm, v(-69.64, -66.35) * mm]});
            skFitSpline(sketch, "E231", {"points": [v(-69.64, -66.35) * mm, v(-69.5, -65.93) * mm, v(-69.83, -65.59) * mm, v(-64.56, -71.64) * mm]});
            skFitSpline(sketch, "E232", {"points": [v(-64.56, -71.64) * mm, v(-58.36, -78.75) * mm, v(-56.3, -80.5) * mm, v(-54.05, -80.5) * mm]});
            skFitSpline(sketch, "E233", {"points": [v(-54.05, -80.5) * mm, v(-53.18, -80.5) * mm, v(-52.63, -80.35) * mm, v(-52.24, -80.03) * mm]});
            skFitSpline(sketch, "E234", {"points": [v(-52.32, -78.88) * mm, v(-52.97, -78.2) * mm, v(-54.03, -75.62) * mm, v(-53.9, -75.04) * mm]});
            skFitSpline(sketch, "E235", {"points": [v(-53.9, -75.04) * mm, v(-53.86, -74.87) * mm, v(-51.44, -76.87) * mm, v(-48.5, -79.48) * mm]});
            skFitSpline(sketch, "E236", {"points": [v(-48.5, -79.48) * mm, v(-43.06, -84.32) * mm, v(-39.84, -86.64) * mm, v(-36.86, -87.85) * mm]});
            skFitSpline(sketch, "E237", {"points": [v(-36.86, -87.85) * mm, v(-35.24, -88.5) * mm, v(-34.68, -88.55) * mm, v(-34.26, -88.04) * mm]});
            skFitSpline(sketch, "E238", {"points": [v(-34.26, -88.04) * mm, v(-34, -87.73) * mm, v(-34.02, -87.52) * mm, v(-34.35, -86.84) * mm]});
            skFitSpline(sketch, "E239", {"points": [v(-34.35, -86.84) * mm, v(-34.56, -86.38) * mm, v(-34.7, -86.01) * mm, v(-34.65, -86.01) * mm]});
            skFitSpline(sketch, "E240", {"points": [v(-34.65, -86.01) * mm, v(-34.6, -86.01) * mm, v(-32.8, -87.11) * mm, v(-30.63, -88.46) * mm]});
            skFitSpline(sketch, "E241", {"points": [v(-30.63, -88.46) * mm, v(-26.24, -91.2) * mm, v(-24.55, -91.93) * mm, v(-20.33, -92.97) * mm]});
            skFitSpline(sketch, "E242", {"points": [v(-20.33, -92.97) * mm, v(-15.07, -94.25) * mm, v(-11.1, -94.76) * mm, v(-6.3, -94.77) * mm]});
            skFitSpline(sketch, "E243", {"points": [v(-6.3, -94.77) * mm, v(-1.62, -94.77) * mm, v(0.3, -94.42) * mm, v(2.94, -93.09) * mm]});
            skFitSpline(sketch, "E244", {"points": [v(2.94, -93.09) * mm, v(3.58, -92.76) * mm, v(4.17, -92.5) * mm, v(4.24, -92.5) * mm]});
            skFitSpline(sketch, "E245", {"points": [v(4.24, -92.5) * mm, v(4.3, -92.5) * mm, v(4.15, -92.84) * mm, v(3.89, -93.27) * mm]});
            skFitSpline(sketch, "E246", {"points": [v(3.89, -93.27) * mm, v(3.63, -93.7) * mm, v(3.41, -94.18) * mm, v(3.41, -94.34) * mm]});
            skFitSpline(sketch, "E247", {"points": [v(3.41, -94.34) * mm, v(3.4, -94.78) * mm, v(4.2, -95.12) * mm, v(5.75, -95.37) * mm]});
            skFitSpline(sketch, "E248", {"points": [v(5.75, -95.37) * mm, v(7.58, -95.65) * mm, v(15.63, -95.5) * mm, v(17.45, -95.13) * mm]});
            skFitSpline(sketch, "E249", {"points": [v(-1.99, -65.46) * mm, v(-20.8, -64.05) * mm, v(-30.47, -61.07) * mm, v(-38.4, -54.24) * mm]});
            skFitSpline(sketch, "E250", {"points": [v(-38.4, -54.24) * mm, v(-45.17, -48.42) * mm, v(-54, -35.38) * mm, v(-58.82, -24.07) * mm]});
            skFitSpline(sketch, "E251", {"points": [v(-58.82, -24.07) * mm, v(-59.76, -21.88) * mm, v(-61.7, -15.76) * mm, v(-64.64, -5.85) * mm]});
            skFitSpline(sketch, "E252", {"points": [v(-64.64, -5.85) * mm, v(-65.56, -2.75) * mm, v(-65.4, -3.06) * mm, v(-71.44, 7.15) * mm]});
            skFitSpline(sketch, "E253", {"points": [v(-71.44, 7.15) * mm, v(-71.65, 7.5) * mm, v(-72.2, 7.97) * mm, v(-72.66, 8.2) * mm]});
            skFitSpline(sketch, "E254", {"points": [v(-72.66, 8.2) * mm, v(-76.08, 9.8) * mm, v(-81.2, 14.1) * mm, v(-83.46, 17.28) * mm]});
            skFitSpline(sketch, "E255", {"points": [v(-85.17, 18.4) * mm, v(-86.23, 16.67) * mm, v(-88.53, 15.85) * mm, v(-88.7, 17.14) * mm]});
            skFitSpline(sketch, "E256", {"points": [v(-88.7, 17.14) * mm, v(-88.8, 17.78) * mm, v(-87.98, 20.64) * mm, v(-87.27, 22.14) * mm]});
            skFitSpline(sketch, "E257", {"points": [v(-87.27, 22.14) * mm, v(-86.7, 23.37) * mm, v(-85.98, 23.7) * mm, v(-83.81, 23.75) * mm]});
            skFitSpline(sketch, "E258", {"points": [v(-82.25, 21.9) * mm, v(-82.3, 20.3) * mm, v(-82.21, 19.83) * mm, v(-81.67, 18.73) * mm]});
            skFitSpline(sketch, "E259", {"points": [v(-81.67, 18.73) * mm, v(-80.48, 16.3) * mm, v(-73.82, 11.85) * mm, v(-69.88, 10.84) * mm]});
            skFitSpline(sketch, "E260", {"points": [v(-69.88, 10.84) * mm, v(-65.8, 9.8) * mm, v(-60.08, 11.02) * mm, v(-51.12, 14.83) * mm]});
            skFitSpline(sketch, "E261", {"points": [v(-51.12, 14.83) * mm, v(-49.23, 15.63) * mm, v(-47.63, 16.23) * mm, v(-47.57, 16.17) * mm]});
            skFitSpline(sketch, "E262", {"points": [v(-47.57, 16.17) * mm, v(-47.4, 16) * mm, v(-49.31, 11.73) * mm, v(-50.17, 10.39) * mm]});
            skFitSpline(sketch, "E263", {"points": [v(-50.17, 10.39) * mm, v(-50.72, 9.52) * mm, v(-50.83, 9.18) * mm, v(-50.6, 9.04) * mm]});
            skFitSpline(sketch, "E264", {"points": [v(-50.6, 9.04) * mm, v(-49.63, 8.44) * mm, v(-44.3, 8.64) * mm, v(-42.27, 9.36) * mm]});
            skFitSpline(sketch, "E265", {"points": [v(-42.27, 9.36) * mm, v(-40.73, 9.9) * mm, v(-38.38, 11.15) * mm, v(-35.99, 12.7) * mm]});
            skFitSpline(sketch, "E266", {"points": [v(-35.99, 12.7) * mm, v(-34.2, 13.86) * mm, v(-33.7, 14.08) * mm, v(-33.53, 13.8) * mm]});
            skFitSpline(sketch, "E267", {"points": [v(-33.53, 13.8) * mm, v(-33.15, 13.2) * mm, v(-33.29, 11.05) * mm, v(-33.78, 9.95) * mm]});
            skFitSpline(sketch, "E268", {"points": [v(-33.78, 9.95) * mm, v(-34.05, 9.38) * mm, v(-34.26, 8.61) * mm, v(-34.26, 8.25) * mm]});
            skFitSpline(sketch, "E269", {"points": [v(-30.97, 7.59) * mm, v(-27.4, 7.6) * mm, v(-24.05, 8.03) * mm, v(-21.7, 8.8) * mm]});
            skFitSpline(sketch, "E270", {"points": [v(-21.7, 8.8) * mm, v(-19.1, 9.68) * mm, v(-13.59, 12.86) * mm, v(-9.66, 15.76) * mm]});
            skFitSpline(sketch, "E271", {"points": [v(-9.66, 15.76) * mm, v(-8.93, 16.3) * mm, v(-8.23, 16.67) * mm, v(-8.1, 16.59) * mm]});
            skFitSpline(sketch, "E272", {"points": [v(-8.1, 16.59) * mm, v(-7.75, 16.36) * mm, v(-7.82, 15.08) * mm, v(-8.25, 14.19) * mm]});
            skFitSpline(sketch, "E273", {"points": [v(-8.25, 14.19) * mm, v(-8.45, 13.75) * mm, v(-9.3, 12.82) * mm, v(-10.1, 12.13) * mm]});
            skFitSpline(sketch, "E274", {"points": [v(-10.1, 12.13) * mm, v(-11.76, 10.74) * mm, v(-12.43, 10.04) * mm, v(-12.43, 9.73) * mm]});
            skFitSpline(sketch, "E275", {"points": [v(-12.43, 9.73) * mm, v(-12.43, 9.43) * mm, v(-11.26, 8.88) * mm, v(-10.23, 8.7) * mm]});
            skFitSpline(sketch, "E276", {"points": [v(-10.23, 8.7) * mm, v(-9.72, 8.6) * mm, v(-8.6, 8.69) * mm, v(-7.6, 8.9) * mm]});
            skFitSpline(sketch, "E277", {"points": [v(-7.6, 8.9) * mm, v(-4.76, 9.5) * mm, v(-1.35, 11.28) * mm, v(3.7, 14.83) * mm]});
            skFitSpline(sketch, "E278", {"points": [v(3.7, 14.83) * mm, v(4.97, 15.73) * mm, v(6.1, 16.47) * mm, v(6.21, 16.46) * mm]});
            skFitSpline(sketch, "E279", {"points": [v(6.21, 16.46) * mm, v(6.32, 16.46) * mm, v(6.73, 16.02) * mm, v(7.13, 15.48) * mm]});
            skFitSpline(sketch, "E280", {"points": [v(7.13, 15.48) * mm, v(7.53, 14.94) * mm, v(8.68, 13.71) * mm, v(9.7, 12.74) * mm]});
            skFitSpline(sketch, "E281", {"points": [v(9.7, 12.74) * mm, v(11.73, 10.8) * mm, v(13.5, 9.83) * mm, v(18.22, 8.1) * mm]});
            skFitSpline(sketch, "E282", {"points": [v(18.22, 8.1) * mm, v(21.44, 6.92) * mm, v(23.48, 6.6) * mm, v(23.72, 7.21) * mm]});
            skFitSpline(sketch, "E283", {"points": [v(23.72, 7.21) * mm, v(23.93, 7.76) * mm, v(23.5, 9.2) * mm, v(22.43, 11.49) * mm]});
            skFitSpline(sketch, "E284", {"points": [v(22.43, 11.49) * mm, v(21.96, 12.51) * mm, v(21.64, 13.42) * mm, v(21.72, 13.5) * mm]});
            skFitSpline(sketch, "E285", {"points": [v(21.72, 13.5) * mm, v(21.8, 13.57) * mm, v(23.03, 12.72) * mm, v(24.46, 11.6) * mm]});
            skFitSpline(sketch, "E286", {"points": [v(24.46, 11.6) * mm, v(25.88, 10.48) * mm, v(28.3, 8.72) * mm, v(29.81, 7.7) * mm]});
            skFitSpline(sketch, "E287", {"points": [v(29.81, 7.7) * mm, v(34.57, 4.47) * mm, v(43.9, 0.39) * mm, v(46.51, 0.39) * mm]});
            skFitSpline(sketch, "E288", {"points": [v(46.51, 0.39) * mm, v(47.92, 0.39) * mm, v(47.87, 2.4) * mm, v(46.38, 5.58) * mm]});
            skFitSpline(sketch, "E289", {"points": [v(46.38, 5.58) * mm, v(45.85, 6.72) * mm, v(45.41, 7.76) * mm, v(45.41, 7.9) * mm]});
            skFitSpline(sketch, "E290", {"points": [v(45.41, 7.9) * mm, v(45.41, 8.02) * mm, v(45.9, 7.68) * mm, v(46.5, 7.13) * mm]});
            skFitSpline(sketch, "E291", {"points": [v(46.5, 7.13) * mm, v(48.93, 4.89) * mm, v(52.05, 3.35) * mm, v(56.7, 2.13) * mm]});
            skFitSpline(sketch, "E292", {"points": [v(56.7, 2.13) * mm, v(58.4, 1.68) * mm, v(59.81, 1.5) * mm, v(62.39, 1.41) * mm]});
            skFitSpline(sketch, "E293", {"points": [v(62.39, 1.41) * mm, v(68.11, 1.2) * mm, v(72.13, 1.94) * mm, v(75.88, 3.88) * mm]});
            skFitSpline(sketch, "E294", {"points": [v(75.88, 3.88) * mm, v(78.46, 5.21) * mm, v(81.98, 7.97) * mm, v(81.8, 8.52) * mm]});
            skFitSpline(sketch, "E295", {"points": [v(81.8, 8.52) * mm, v(81.11, 10.59) * mm, v(81.08, 10.9) * mm, v(81.5, 11.52) * mm]});
            skFitSpline(sketch, "E296", {"points": [v(81.5, 11.52) * mm, v(82.1, 12.46) * mm, v(83.55, 12.4) * mm, v(84.38, 11.42) * mm]});
            skFitSpline(sketch, "E297", {"points": [v(84.38, 11.42) * mm, v(84.72, 11.02) * mm, v(85.11, 10.3) * mm, v(85.26, 9.8) * mm]});
            skFitSpline(sketch, "E298", {"points": [v(85.26, 9.8) * mm, v(85.6, 8.67) * mm, v(85.87, 3.5) * mm, v(85.6, 3.5) * mm]});
            skFitSpline(sketch, "E299", {"points": [v(85.6, 3.5) * mm, v(85.48, 3.5) * mm, v(84.87, 4.02) * mm, v(84.23, 4.65) * mm]});
            skFitSpline(sketch, "E300", {"points": [v(82.44, 4.95) * mm, v(79.74, 1.39) * mm, v(76.92, -0.16) * mm, v(70.9, -1.37) * mm]});
            skFitSpline(sketch, "E301", {"points": [v(66.96, -4.53) * mm, v(64.2, -9.85) * mm, v(61.97, -14.97) * mm, v(60.16, -20.13) * mm]});
            skFitSpline(sketch, "E302", {"points": [v(60.16, -20.13) * mm, v(57.35, -28.15) * mm, v(56.61, -29.89) * mm, v(54.24, -34.05) * mm]});
            skFitSpline(sketch, "E303", {"points": [v(54.24, -34.05) * mm, v(49.72, -42.01) * mm, v(44.5, -49.27) * mm, v(40.67, -52.92) * mm]});
            skFitSpline(sketch, "E304", {"points": [v(40.67, -52.92) * mm, v(34.44, -58.87) * mm, v(24.27, -63.42) * mm, v(13.61, -65.04) * mm]});
            skFitSpline(sketch, "E305", {"points": [v(13.61, -65.04) * mm, v(11.31, -65.4) * mm, v(0.83, -65.68) * mm, v(-1.99, -65.46) * mm]});
            skFitSpline(sketch, "E306", {"points": [v(37.09, 40.81) * mm, v(46.02, 43.08) * mm, v(53.09, 50.19) * mm, v(55.48, 59.3) * mm]});
            skFitSpline(sketch, "E307", {"points": [v(55.48, 59.3) * mm, v(57.78, 68.13) * mm, v(55.45, 77.37) * mm, v(49.15, 84.33) * mm]});
            skFitSpline(sketch, "E308", {"points": [v(49.15, 84.33) * mm, v(46.51, 87.24) * mm, v(41.5, 90.25) * mm, v(37.35, 91.4) * mm]});
            skFitSpline(sketch, "E309", {"points": [v(37.35, 91.4) * mm, v(35.72, 91.85) * mm, v(34.84, 91.92) * mm, v(31.13, 91.92) * mm]});
            skFitSpline(sketch, "E310", {"points": [v(31.13, 91.92) * mm, v(25.97, 91.92) * mm, v(24.45, 91.59) * mm, v(20.33, 89.56) * mm]});
            skFitSpline(sketch, "E311", {"points": [v(20.33, 89.56) * mm, v(14.23, 86.56) * mm, v(9.8, 81.52) * mm, v(7.41, 74.87) * mm]});
            skFitSpline(sketch, "E312", {"points": [v(7.41, 74.87) * mm, v(6.47, 72.23) * mm, v(6.03, 69.49) * mm, v(6.03, 66.13) * mm]});
            skFitSpline(sketch, "E313", {"points": [v(6.03, 66.13) * mm, v(6.02, 58.58) * mm, v(8.7, 52.16) * mm, v(14, 47.05) * mm]});
            skFitSpline(sketch, "E314", {"points": [v(14, 47.05) * mm, v(17.85, 43.35) * mm, v(22.72, 40.97) * mm, v(27.95, 40.23) * mm]});
            skFitSpline(sketch, "E315", {"points": [v(27.95, 40.23) * mm, v(30.36, 39.89) * mm, v(34.49, 40.15) * mm, v(37.09, 40.81) * mm]});
            skFitSpline(sketch, "E316", {"points": [v(21.2, 60.77) * mm, v(15, 62.44) * mm, v(12, 69.12) * mm, v(14.86, 74.94) * mm]});
            skFitSpline(sketch, "E317", {"points": [v(14.86, 74.94) * mm, v(15.74, 76.74) * mm, v(18.08, 78.9) * mm, v(19.9, 79.6) * mm]});
            skFitSpline(sketch, "E318", {"points": [v(19.9, 79.6) * mm, v(26.56, 82.15) * mm, v(33.65, 77.4) * mm, v(33.65, 70.37) * mm]});
            skFitSpline(sketch, "E319", {"points": [v(33.65, 70.37) * mm, v(33.65, 63.9) * mm, v(27.42, 59.1) * mm, v(21.2, 60.77) * mm]});
            skFitSpline(sketch, "E320", {"points": [v(-15.6, 44.2) * mm, v(-6.12, 46) * mm, v(1.55, 52.8) * mm, v(4.46, 62) * mm]});
            skFitSpline(sketch, "E321", {"points": [v(4.46, 62) * mm, v(5.31, 64.71) * mm, v(5.61, 66.76) * mm, v(5.61, 69.9) * mm]});
            skFitSpline(sketch, "E322", {"points": [v(5.61, 69.9) * mm, v(5.61, 77.15) * mm, v(2.82, 83.65) * mm, v(-2.44, 88.65) * mm]});
            skFitSpline(sketch, "E323", {"points": [v(-2.44, 88.65) * mm, v(-5.69, 91.73) * mm, v(-9.66, 93.95) * mm, v(-14.04, 95.12) * mm]});
            skFitSpline(sketch, "E324", {"points": [v(-14.04, 95.12) * mm, v(-16.12, 95.67) * mm, v(-16.84, 95.75) * mm, v(-20.35, 95.75) * mm]});
            skFitSpline(sketch, "E325", {"points": [v(-20.35, 95.75) * mm, v(-23.86, 95.75) * mm, v(-24.58, 95.67) * mm, v(-26.66, 95.12) * mm]});
            skFitSpline(sketch, "E326", {"points": [v(-26.66, 95.12) * mm, v(-34.34, 93.07) * mm, v(-40.75, 87.73) * mm, v(-44, 80.68) * mm]});
            skFitSpline(sketch, "E327", {"points": [v(-44, 80.68) * mm, v(-47.58, 72.95) * mm, v(-47.1, 63.86) * mm, v(-42.74, 56.52) * mm]});
            skFitSpline(sketch, "E328", {"points": [v(-42.74, 56.52) * mm, v(-38.99, 50.2) * mm, v(-32.51, 45.65) * mm, v(-25.24, 44.2) * mm]});
            skFitSpline(sketch, "E329", {"points": [v(-25.24, 44.2) * mm, v(-22.97, 43.75) * mm, v(-17.96, 43.74) * mm, v(-15.6, 44.2) * mm]});
            skFitSpline(sketch, "E330", {"points": [v(-16.74, 53.08) * mm, v(-19.51, 53.85) * mm, v(-21.71, 55.71) * mm, v(-23.03, 58.4) * mm]});
            skFitSpline(sketch, "E331", {"points": [v(-23.03, 58.4) * mm, v(-23.68, 59.71) * mm, v(-23.82, 60.3) * mm, v(-23.9, 62.06) * mm]});
            skFitSpline(sketch, "E332", {"points": [v(-23.9, 62.06) * mm, v(-24.03, 64.64) * mm, v(-23.6, 66.25) * mm, v(-22.29, 68.23) * mm]});
            skFitSpline(sketch, "E333", {"points": [v(-22.29, 68.23) * mm, v(-18.77, 73.5) * mm, v(-10.99, 74.1) * mm, v(-6.77, 69.44) * mm]});
            skFitSpline(sketch, "E334", {"points": [v(-6.77, 69.44) * mm, v(-2.16, 64.34) * mm, v(-3.72, 56.53) * mm, v(-9.93, 53.63) * mm]});
            skFitSpline(sketch, "E335", {"points": [v(-9.93, 53.63) * mm, v(-11.86, 52.72) * mm, v(-14.66, 52.5) * mm, v(-16.74, 53.08) * mm]});
            skSolve(sketch);
        }
        {
            var Q0;
            Q0=makeQuery(id+"F0.imprint","IMPRINT",FACE,{"disambiguationData":[TD([[makeQuery(id+"F0.imprint","IMPRINT",EDGE,{"derivedFrom":sQuery(id+"F0.wireOp",EDGE,"E0")}),-1.0]])]});
            var Q1;
            Q1=makeQuery(id+"F0.imprint","IMPRINT",FACE,{"disambiguationData":[TD([[makeQuery(id+"F0.imprint","IMPRINT",EDGE,{"derivedFrom":sQuery(id+"F0.wireOp",EDGE,"E12")}),1.0]])]});
            var Q2;
            Q2=makeQuery(id+"F0.imprint","IMPRINT",FACE,{"disambiguationData":[TD([[makeQuery(id+"F0.imprint","IMPRINT",EDGE,{"derivedFrom":sQuery(id+"F0.wireOp",EDGE,"E330")}),-1.0]])]});
            var Q3;
            Q3=makeQuery(id+"F0.imprint","IMPRINT",FACE,{"disambiguationData":[TD([[makeQuery(id+"F0.imprint","IMPRINT",EDGE,{"derivedFrom":sQuery(id+"F0.wireOp",EDGE,"E316")}),-1.0]])]});
            extrude(context, id + "F1", {"entities" : qUnion([Q0, Q1, Q2, Q3]), "depth" : 30 * mm, "offsetDistance" : 25 * mm});
        }
        {
            var Q0;
            Q0=makeQuery(id+"F0.imprint","IMPRINT",FACE,{"disambiguationData":[TD([[makeQuery(id+"F0.imprint","IMPRINT",EDGE,{"derivedFrom":sQuery(id+"F0.wireOp",EDGE,"E24")}),-1.0]])]});
            var Q1;
            Q1=makeQuery(id+"F0.imprint","IMPRINT",FACE,{"disambiguationData":[TD([[makeQuery(id+"F0.imprint","IMPRINT",EDGE,{"derivedFrom":sQuery(id+"F0.wireOp",EDGE,"E320")}),1.0]])]});
            var Q2;
            Q2=makeQuery(id+"F0.imprint","IMPRINT",FACE,{"disambiguationData":[TD([[makeQuery(id+"F0.imprint","IMPRINT",EDGE,{"derivedFrom":sQuery(id+"F0.wireOp",EDGE,"E306")}),1.0]])]});
            extrude(context, id + "F2", {"entities" : qUnion([Q0, Q1, Q2]), "depth" : 15 * mm, "offsetDistance" : 25 * mm});
        }
    });
